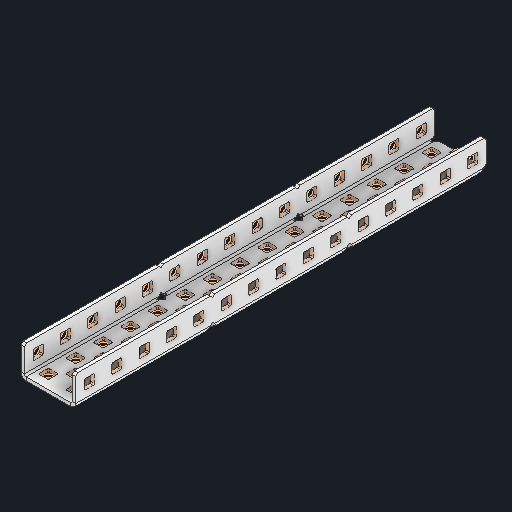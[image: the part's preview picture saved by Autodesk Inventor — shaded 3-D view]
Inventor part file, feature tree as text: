
AUTODESK INVENTOR PART (.ipt)
format: ipt  version: 2024 (Build 280153000, 153)  size: 1,115,648 bytes
history: native  units: in
note: dims shown in document units (in); Inventor stores cm internally (conversion verified against a paired STEP export)
features: other x82, extrude x73, sheet_metal_op x11, pattern_linear x2, mirror x1, chamfer x1, sketch x1
ambient origin geometry x8: Origin, YZ Plane, XZ Plane, XY Plane, X Axis, Y Axis, Z Axis, Center Point
bodies: Solid1 (feature_tree), Body (feature_tree)
feature tree (171):
  sheet_metal_op  "Flanges"
  other  "Flange Pattern Plane"
  other  "Flange Pattern Sketch"
  sheet_metal_op  "Flange Pattern"
  sheet_metal_op  "Body Pattern"
  pattern_linear  "Center Pattern"  Spacing1=7.5in  [1 undecoded]
  other  "Arc Length"
  mirror  "Notch Mirror"
  pattern_linear  "Notch Pattern"  Spacing1=0.0625in  [1 undecoded]
  chamfer  "End Chamfer"
  extrude  "Half Cut"  Depth=0.0625in
  other  "Plate1"
  sketch  "Sketch2"  dims[d0=1.0in d1=7.5in d2=0.0625in d3=0.0625in d4=0.0312in d5=0.125in d6=0.0625in d7=0.5in d8=90.0deg d9=0.0312in d10=0.25in d11=0.0625in d12=0.0625in d16=0.182in d17=0.02in d18=0.0625in d19=0.0in d20=0.25in d21=0.25in d38=5.9055in d40=0.5in d41=0.7874in d43=1.0in d46=0.172in d47=1.0in d48=0.0in d49=0.182in d50=0.02in d51=0.25in d52=0.25in d53=0.0625in d54=0.0in d55=0.172in d56=1.0in d57=0.0in d58=0.25in d60=5.9055in d62=0.5in d63=0.7874in d65=0.5in d85=0.1473in d86=0.1782in d88=0.04in d89=0.0625in d90=0.0in d91=0.04in d92=0.0491in d95=2.5in d96=0.04in d97=0.25in d98=45.0deg d99=0.25in d100=0.5in d101=0.0in d102=2.497in d106=0.182in d107=0.02in d108=0.5in d109=0.5in d110=0.0625in d111=0.0in d112=0.172in d113=0.5in d114=0.0in d117=0.5in d118=0.5in d119=0.5in]
  other  "Plate2"
  sheet_metal_op  "Bend1"
  sheet_metal_op  "Corner1"
  other  "Srf1"
  other  "Srf2"
  other  "Srf91"
  sheet_metal_op  "Body Pattern Sketch"
  other  "Srf92"
  other  "Srf786"
  other  "Srf823"
  other  "Srf824"
  other  "Srf825"
  other  "Srf826"
  other  "Srf827"
  other  "Srf828"
  other  "Srf829"
  other  "Srf856"
  other  "Srf857"
  other  "Srf858"
  other  "Srf859"
  other  "Srf860"
  other  "Srf861"
  other  "Srf862"
  other  "Srf889"
  other  "Srf890"
  other  "Srf891"
  other  "Srf892"
  other  "Srf893"
  other  "Srf894"
  other  "Srf895"
  other  "Srf896"
  other  "Srf922"
  other  "Srf923"
  other  "Srf924"
  other  "Srf925"
  other  "Srf926"
  other  "Srf959"
  other  "Srf960"
  other  "Srf961"
  other  "Srf962"
  other  "Srf963"
  other  "Srf996"
  other  "Srf997"
  other  "Srf998"
  other  "Srf999"
  other  "Srf1000"
  other  "Srf1143"
  other  "Srf1144"
  other  "Srf1145"
  other  "Srf1146"
  other  "Srf1147"
  other  "Srf1148"
  other  "Srf1149"
  other  "Srf1150"
  other  "Srf1151"
  other  "Srf1152"
  other  "Srf1153"
  other  "Srf1154"
  other  "Srf1155"
  other  "Srf1156"
  other  "Srf1157"
  other  "Srf1158"
  other  "Srf1199"
  other  "Srf1200"
  other  "Srf1201"
  other  "Srf1202"
  other  "Srf1203"
  other  "Srf1204"
  other  "Srf1205"
  other  "Srf1206"
  other  "Srf1207"
  other  "Srf1208"
  other  "Srf1209"
  other  "Srf1210"
  other  "Srf1211"
  other  "Srf1212"
  other  "Srf1213"
  other  "Srf1214"
  other  "Srf1255"
  sheet_metal_op  "Flange Stamp"
  sheet_metal_op  "Flange Circle"
  sheet_metal_op  "Body Stamp"
  sheet_metal_op  "Body Circle"
  other  "Center Stamp"
  other  "Center Circle"
  sheet_metal_op  "Notch"
  extrude  "ExtrusionSrf2"  Depth=0.0312in
  extrude  "ExtrusionSrf92"  Depth=0.5in
  extrude  "ExtrusionSrf823"  Depth=0.0625in
  extrude  "ExtrusionSrf824"  Depth=0.5in TaperAngle=90.0deg
  extrude  "ExtrusionSrf825"  Depth=0.5in
  extrude  "ExtrusionSrf826"  Depth=0.0625in
  extrude  "ExtrusionSrf827"  Depth=0.0625in
  extrude  "ExtrusionSrf828"  Depth=0.5in
  extrude  "ExtrusionSrf829"  Depth=0.02in
  extrude  "ExtrusionSrf856"  Depth=0.0625in
  extrude  "ExtrusionSrf857"  TaperAngle=0.0deg  [1 undecoded]
  extrude  "ExtrusionSrf858"  Depth=0.5in
  extrude  "ExtrusionSrf859"  Depth=0.5in
  extrude  "ExtrusionSrf860"  Depth=0.5in
  extrude  "ExtrusionSrf861"  Depth=0.5in
  extrude  "ExtrusionSrf862"  Depth=1.0in TaperAngle=0.0deg
  extrude  "ExtrusionSrf889"  Depth=0.5in
  extrude  "ExtrusionSrf890"  Depth=0.02in
  extrude  "ExtrusionSrf891"  Depth=0.5in
  extrude  "ExtrusionSrf892"  Depth=0.5in
  extrude  "ExtrusionSrf893"  Depth=0.0625in
  extrude  "ExtrusionSrf894"  TaperAngle=0.0deg  [1 undecoded]
  extrude  "ExtrusionSrf895"  Depth=0.5in
  extrude  "ExtrusionSrf896"  Depth=1.0in TaperAngle=0.0deg
  extrude  "ExtrusionSrf922"  Depth=0.5in
  extrude  "ExtrusionSrf923"  Depth=0.5in
  extrude  "ExtrusionSrf924"  Depth=0.5in
  extrude  "ExtrusionSrf925"  Depth=0.5in
  extrude  "ExtrusionSrf926"  Depth=0.5in
  extrude  "ExtrusionSrf959"  Depth=0.5in
  extrude  "ExtrusionSrf960"  Depth=0.0625in
  extrude  "ExtrusionSrf961"  TaperAngle=0.0deg  [1 undecoded]
  extrude  "ExtrusionSrf962"  Depth=0.5in
  extrude  "ExtrusionSrf963"  Depth=0.5in
  extrude  "ExtrusionSrf996"  Depth=2.5in
  extrude  "ExtrusionSrf997"  Depth=0.5in TaperAngle=45.0deg
  extrude  "ExtrusionSrf998"  Depth=0.5in
  extrude  "ExtrusionSrf999"  Depth=0.5in TaperAngle=0.0deg
  extrude  "ExtrusionSrf1000"  Depth=0.5in
  extrude  "ExtrusionSrf1143"  Depth=0.5in
  extrude  "ExtrusionSrf1144"  Depth=0.02in
  extrude  "ExtrusionSrf1145"  Depth=0.5in
  extrude  "ExtrusionSrf1146"  Depth=0.5in
  extrude  "ExtrusionSrf1147"  Depth=0.0625in
  extrude  "ExtrusionSrf1148"  TaperAngle=0.0deg  [1 undecoded]
  extrude  "ExtrusionSrf1149"  Depth=0.5in
  extrude  "ExtrusionSrf1150"  Depth=0.5in TaperAngle=0.0deg
  extrude  "ExtrusionSrf1151"  Depth=0.5in
  extrude  "ExtrusionSrf1152"  Depth=0.5in
  extrude  "ExtrusionSrf1153"  Depth=0.5in
  extrude  "ExtrusionSrf1154"  [1 undecoded]
  extrude  "ExtrusionSrf1155"  [1 undecoded]
  extrude  "ExtrusionSrf1156"  [1 undecoded]
  extrude  "ExtrusionSrf1157"  [1 undecoded]
  extrude  "ExtrusionSrf1158"  [1 undecoded]
  extrude  "ExtrusionSrf1199"  [1 undecoded]
  extrude  "ExtrusionSrf1200"  [1 undecoded]
  extrude  "ExtrusionSrf1201"  [1 undecoded]
  extrude  "ExtrusionSrf1202"  [1 undecoded]
  extrude  "ExtrusionSrf1203"  [1 undecoded]
  extrude  "ExtrusionSrf1204"  [1 undecoded]
  extrude  "ExtrusionSrf1205"  [1 undecoded]
  extrude  "ExtrusionSrf1206"  [1 undecoded]
  extrude  "ExtrusionSrf1207"  [1 undecoded]
  extrude  "ExtrusionSrf1208"  [1 undecoded]
  extrude  "ExtrusionSrf1209"  [1 undecoded]
  extrude  "ExtrusionSrf1210"  [1 undecoded]
  extrude  "ExtrusionSrf1211"  [1 undecoded]
  extrude  "ExtrusionSrf1212"  [1 undecoded]
  extrude  "ExtrusionSrf1213"  [1 undecoded]
  extrude  "ExtrusionSrf1214"  [1 undecoded]
  extrude  "ExtrusionSrf1255"  [1 undecoded]
note: 28 required parameter values undecoded (feature->parameter linkage not recoverable at this tier; creation-order binding heuristic only, values carry confidence <= 0.55)
